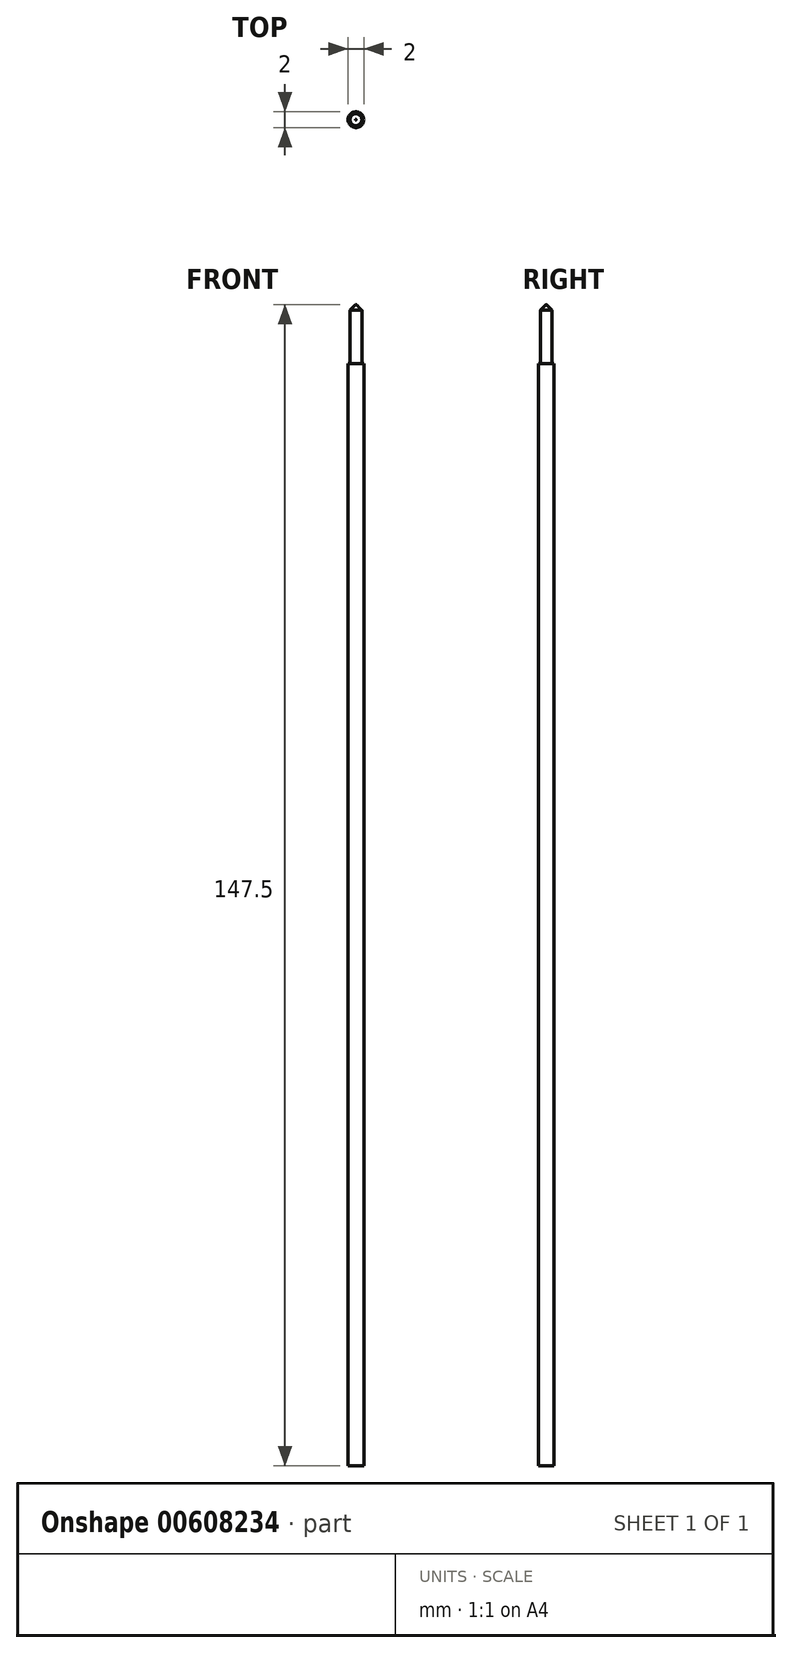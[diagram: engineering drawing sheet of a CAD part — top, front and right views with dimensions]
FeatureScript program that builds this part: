
annotation { "Feature Type Name" : "Feature", "Feature Type Description" : "" }
export const myFeature = defineFeature(function(context is Context, id is Id, definition is map)
    precondition{}
    {
        {
            var Q0;
            Q0=qCreatedBy(makeId("Top.planeOp"),FACE);
            var sketch = newSketch(context, id + "F0", { "sketchPlane" : qUnion([Q0])});
            skCircle(sketch, "E0", {"center": v(0, 0) * mm, "radius": 1 * mm});
            skSolve(sketch);
        }
        {
            var Q0;
            Q0=makeQuery(id+"F0.imprint","IMPRINT",FACE,{"disambiguationData":[TD([[makeQuery(id+"F0.imprint","IMPRINT",EDGE,{"derivedFrom":sQuery(id+"F0.wireOp",EDGE,"E0")}),1.0]])]});
            extrude(context, id + "F1", {"entities" : qUnion([Q0]), "depth" : 140 * mm, "offsetDistance" : 25 * mm});
        }
        {
            var Q0;
            Q0=makeQuery(id+"F1.opExtrude","CAP_FACE",FACE,{"disambiguationData":[OSD([sQuery(id+"F0.wireOp",EDGE,"E0")])],"isStart":false});
            var sketch = newSketch(context, id + "F2", { "sketchPlane" : qUnion([Q0])});
            skCircle(sketch, "E1", {"center": v(0, 0) * mm, "radius": 0.75 * mm});
            skSolve(sketch);
        }
        {
            var Q0;
            Q0=makeQuery(id+"F2.imprint","IMPRINT",FACE,{"disambiguationData":[TD([[makeQuery(id+"F2.imprint","IMPRINT",EDGE,{"derivedFrom":sQuery(id+"F2.wireOp",EDGE,"E1")}),1.0]])]});
            extrude(context, id + "F3", {"entities" : qUnion([Q0]), "operationType" : NewBodyOperationType.ADD, "depth" : 7.5 * mm, "offsetDistance" : 25 * mm});
        }
        {
            var Q0;
            Q0=makeQuery(id+"F3.opExtrude","CAP_EDGE",EDGE,{"disambiguationData":[OSD([sQuery(id+"F2.wireOp",EDGE,"E1")])],"isStart":false});
            chamfer(context, id + "F4", {"entities" : qUnion([Q0]), "width" : 0.7 * mm, "tangentPropagation" : true});
        }
    });
